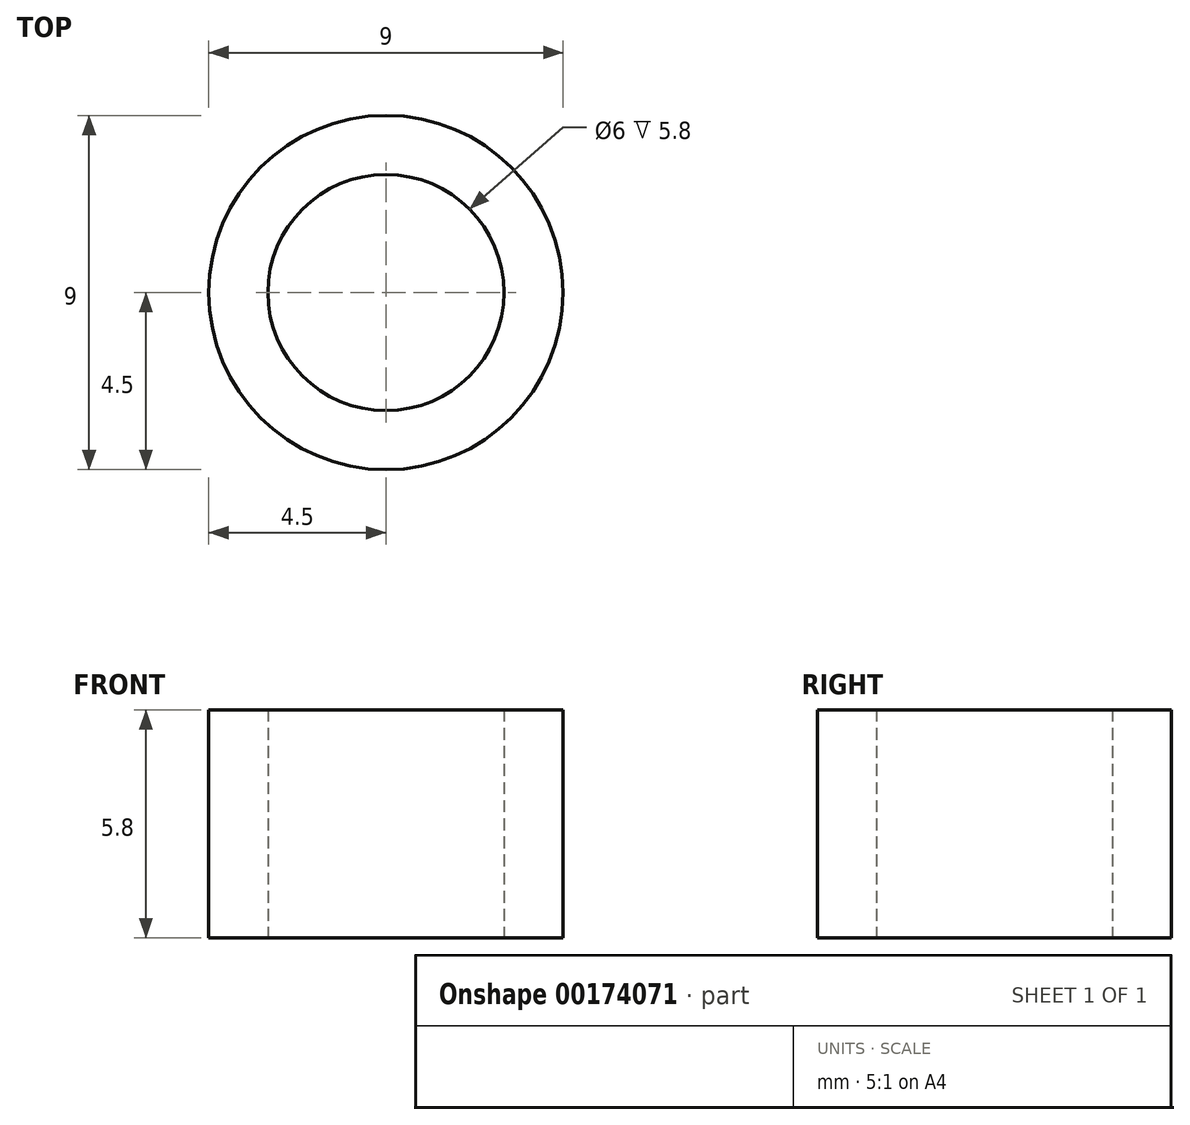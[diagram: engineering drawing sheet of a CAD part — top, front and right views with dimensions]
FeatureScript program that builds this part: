
annotation { "Feature Type Name" : "Feature", "Feature Type Description" : "" }
export const myFeature = defineFeature(function(context is Context, id is Id, definition is map)
    precondition{}
    {
        {
            var Q0;
            Q0=qCreatedBy(makeId("Top.planeOp"),FACE);
            var sketch = newSketch(context, id + "F0", { "sketchPlane" : qUnion([Q0])});
            skCircle(sketch, "E0", {"center": v(0, 0) * mm, "radius": 4.5 * mm});
            skCircle(sketch, "E1", {"center": v(0, 0) * mm, "radius": 3 * mm});
            skSolve(sketch);
        }
        {
            var Q0;
            Q0=makeQuery(id+"F0.imprint","IMPRINT",FACE,{"disambiguationData":[TD([[makeQuery(id+"F0.imprint","IMPRINT",EDGE,{"derivedFrom":sQuery(id+"F0.wireOp",EDGE,"E0")}),1.0]])]});
            extrude(context, id + "F1", {"entities" : qUnion([Q0]), "depth" : 5.8 * mm});
        }
    });
